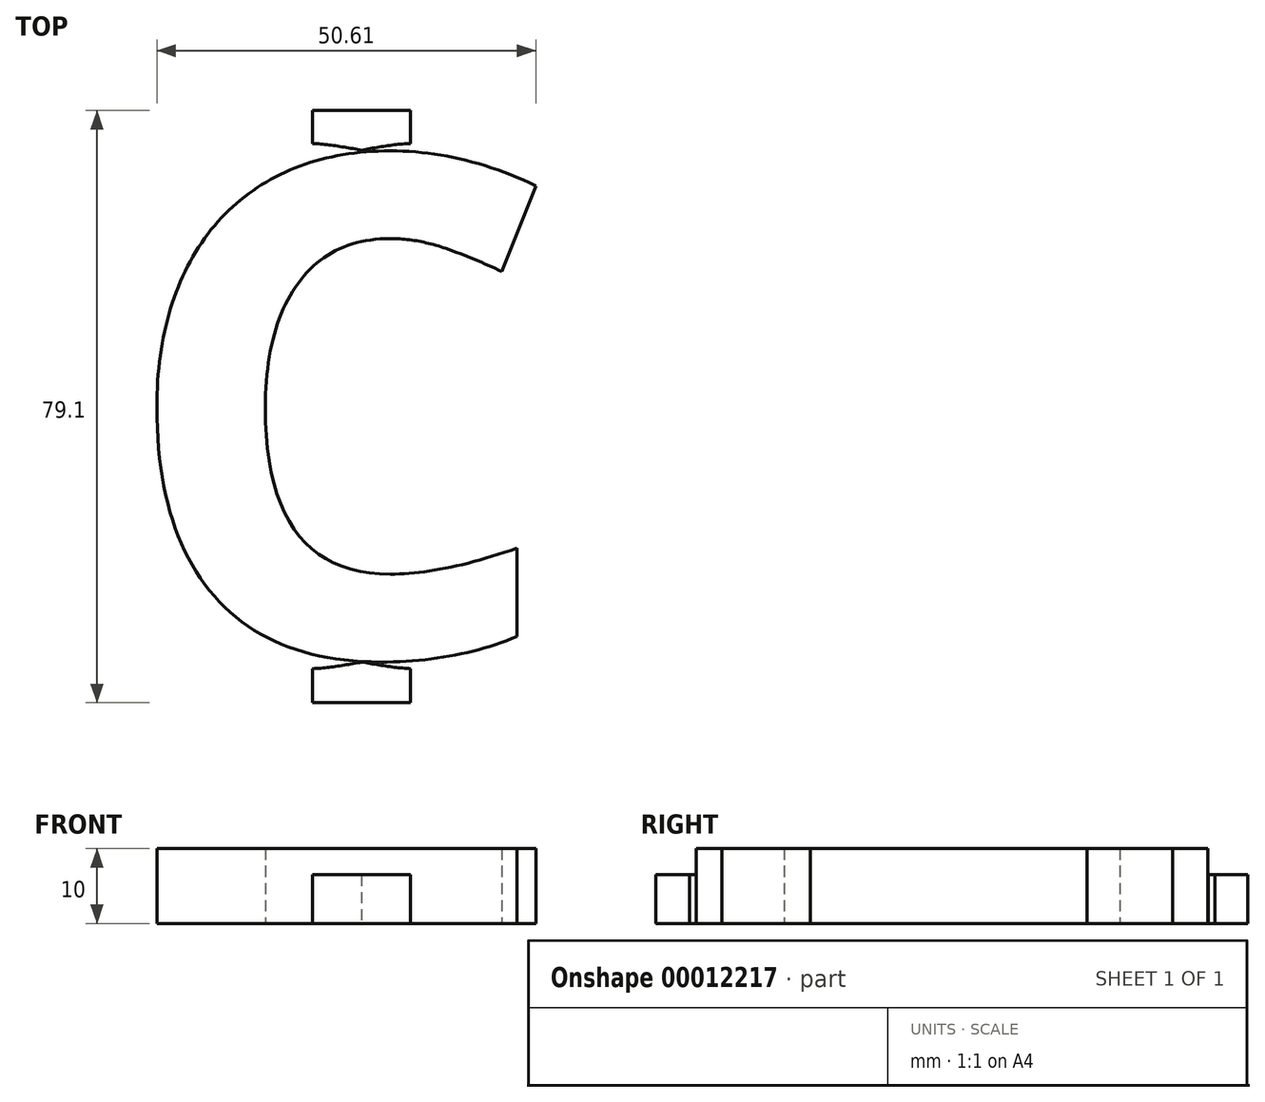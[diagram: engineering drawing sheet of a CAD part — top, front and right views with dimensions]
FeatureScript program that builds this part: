
annotation { "Feature Type Name" : "Feature", "Feature Type Description" : "" }
export const myFeature = defineFeature(function(context is Context, id is Id, definition is map)
    precondition{}
    {
        {
            var Q0;
            Q0=qCreatedBy(makeId("Top.planeOp"),FACE);
            var sketch = newSketch(context, id + "F0", { "sketchPlane" : qUnion([Q0])});
            skText(sketch, "E0", { "text": "C", "fontName": "OpenSans-Bold.ttf"});
            const initialGuessF0  = {"E0": [-0.05602, 0, 1, 0, 0.067]};
            skSetInitialGuess(sketch, initialGuessF0);
            skSolve(sketch);
        }
        {
            var Q0;
            Q0=makeQuery(id+"F0.imprint","IMPRINT",FACE,{"disambiguationData":[TD([[makeQuery(id+"F0.imprint","IMPRINT",EDGE,{"derivedFrom":sQuery(id+"F0.wireOp",EDGE,"E0.sketch_text.stroke-0")}),-1.0]])]});
            extrude(context, id + "F1", {"entities" : qUnion([Q0]), "depth" : 10 * mm});
        }
        {
            var Q0;
            Q0=qCreatedBy(makeId("Top.planeOp"),FACE);
            var sketch = newSketch(context, id + "F2", { "sketchPlane" : qUnion([Q0])});
            skFitSpline(sketch, "E1.0.0", {"points": [v(-5.7, 7.45) * mm, v(0, 15.82) * mm, v(0, 33.2) * mm]});
            skFitSpline(sketch, "E1.0.1", {"points": [v(0, 33.2) * mm, v(0, 50.03) * mm, v(-5.88, 58.76) * mm, v(0, 33.2) * mm]});
            skFitSpline(sketch, "E1.0.2", {"points": [v(-5.88, 58.76) * mm, v(-11.76, 67.48) * mm, v(-23.26, 67.48) * mm]});
            skFitSpline(sketch, "E1.0.3", {"points": [v(-23.26, 67.48) * mm, v(-35.07, 67.48) * mm, v(-40.76, 59.14) * mm]});
            skFitSpline(sketch, "E1.0.4", {"points": [v(-40.76, 59.14) * mm, v(-46.44, 50.8) * mm, v(-46.44, 33.2) * mm]});
            skFitSpline(sketch, "E1.0.5", {"points": [v(-46.44, 33.2) * mm, v(-46.44, 16.36) * mm, v(-40.6, 7.72) * mm]});
            skFitSpline(sketch, "E1.0.6", {"points": [v(-40.6, 7.72) * mm, v(-34.76, -0.92) * mm, v(-23.26, -0.92) * mm]});
            skFitSpline(sketch, "E1.0.7", {"points": [v(-23.26, -0.92) * mm, v(-11.4, -0.92) * mm, v(-5.7, 7.45) * mm]});
            skLineSegment(sketch, "E2", {"start": v(-46.44, 33.2) * mm, "end": v(-46.44, 67.48) * mm, "construction": true});
            skLineSegment(sketch, "E3", {"start": v(-46.44, 67.48) * mm, "end": v(-23.26, 67.48) * mm, "construction": true});
            skLineSegment(sketch, "E4", {"start": v(-23.26, 67.48) * mm, "end": v(0, 67.48) * mm, "construction": true});
            skLineSegment(sketch, "E5", {"start": v(0, 67.48) * mm, "end": v(0, 33.2) * mm, "construction": true});
            skLineSegment(sketch, "E6", {"start": v(0, 33.03) * mm, "end": v(0, 0) * mm, "construction": true});
            skLineSegment(sketch, "E7", {"start": v(0, 33.03) * mm, "end": v(-36.12, 33.03) * mm, "construction": true});
            skLineSegment(sketch, "E8", {"start": v(-2.5, 33.03) * mm, "end": v(-36.12, 33.03) * mm, "construction": true});
            skLineSegment(sketch, "E9", {"start": v(-2.5, 14.3) * mm, "end": v(-2.5, 33.03) * mm, "construction": true});
            skLineSegment(sketch, "E10", {"start": v(-2.5, 0) * mm, "end": v(0, 0) * mm, "construction": true});
            skLineSegment(sketch, "E11", {"start": v(-46.44, 66.36) * mm, "end": v(0, 66.36) * mm, "construction": true});
            skLineSegment(sketch, "E12.bottom", {"start": v(-23.26, 66.36) * mm, "end": v(-29.8, 66.36) * mm});
            skLineSegment(sketch, "E12.top", {"start": v(-23.26, 72.76) * mm, "end": v(-29.8, 72.76) * mm});
            skLineSegment(sketch, "E12.left", {"start": v(-23.26, 66.36) * mm, "end": v(-23.26, 72.76) * mm});
            skLineSegment(sketch, "E12.right", {"start": v(-29.8, 66.36) * mm, "end": v(-29.8, 72.76) * mm});
            skLineSegment(sketch, "E13.bottom", {"start": v(-23.26, 66.36) * mm, "end": v(-16.72, 66.36) * mm});
            skLineSegment(sketch, "E13.top", {"start": v(-23.26, 72.76) * mm, "end": v(-16.72, 72.76) * mm});
            skLineSegment(sketch, "E13.right", {"start": v(-16.72, 66.36) * mm, "end": v(-16.72, 72.76) * mm});
            skLineSegment(sketch, "E14", {"start": v(-46.44, 33.2) * mm, "end": v(0, 33.2) * mm, "construction": true});
            skLineSegment(sketch, "E15", {"start": v(-46.44, 33.2) * mm, "end": v(0, 33.2) * mm});
            skLineSegment(sketch, "E16.0.MirrorCS", {"start": v(-23.26, -6.34) * mm, "end": v(-16.72, -6.34) * mm});
            skLineSegment(sketch, "E16.1.MirrorCS", {"start": v(-23.26, -6.34) * mm, "end": v(-29.8, -6.34) * mm});
            skLineSegment(sketch, "E16.2.MirrorCS", {"start": v(-16.72, 0.06) * mm, "end": v(-16.72, -6.34) * mm});
            skLineSegment(sketch, "E16.3.MirrorCS", {"start": v(-23.26, 0.06) * mm, "end": v(-16.72, 0.06) * mm});
            skLineSegment(sketch, "E16.4.MirrorCS", {"start": v(-23.26, 0.06) * mm, "end": v(-23.26, -6.34) * mm});
            skLineSegment(sketch, "E16.5.MirrorCS", {"start": v(-23.26, 0.06) * mm, "end": v(-29.8, 0.06) * mm});
            skLineSegment(sketch, "E16.6.MirrorCS", {"start": v(-29.8, 0.06) * mm, "end": v(-29.8, -6.34) * mm});
            skLineSegment(sketch, "E16.7.MirrorCS", {"start": v(-23.26, 0.06) * mm, "end": v(-23.26, -6.34) * mm});
            skSolve(sketch);
        }
        {
            var Q0;
            {var subQ1=sQuery(id+"F2.wireOp",EDGE,"E12.top");Q0=makeQuery(id+"F2.imprint","IMPRINT",FACE,{"disambiguationData":[TD([[makeQuery(id+"F2.imprint","IMPRINT",EDGE,{"derivedFrom":subQ1}),1.0]])]});}
            var Q1;
            {var subQ3=sQuery(id+"F2.wireOp",EDGE,"E13.top");Q1=makeQuery(id+"F2.imprint","IMPRINT",FACE,{"disambiguationData":[TD([[makeQuery(id+"F2.imprint","IMPRINT",EDGE,{"derivedFrom":subQ3}),-1.0]])]});}
            extrude(context, id + "F3", {"entities" : qUnion([Q0, Q1]), "operationType" : NewBodyOperationType.ADD, "depth" : 6.5 * mm});
        }
        {
            var Q0;
            {var subQ3=sQuery(id+"F2.wireOp",EDGE,"E16.1.MirrorCS");Q0=makeQuery(id+"F2.imprint","IMPRINT",FACE,{"disambiguationData":[TD([[makeQuery(id+"F2.imprint","IMPRINT",EDGE,{"derivedFrom":subQ3}),-1.0]])]});}
            var Q1;
            {var subQ1=sQuery(id+"F2.wireOp",EDGE,"E16.0.MirrorCS");Q1=makeQuery(id+"F2.imprint","IMPRINT",FACE,{"disambiguationData":[TD([[makeQuery(id+"F2.imprint","IMPRINT",EDGE,{"derivedFrom":subQ1}),1.0]])]});}
            extrude(context, id + "F4", {"entities" : qUnion([Q0, Q1]), "operationType" : NewBodyOperationType.ADD, "depth" : 6.5 * mm});
        }
    });
